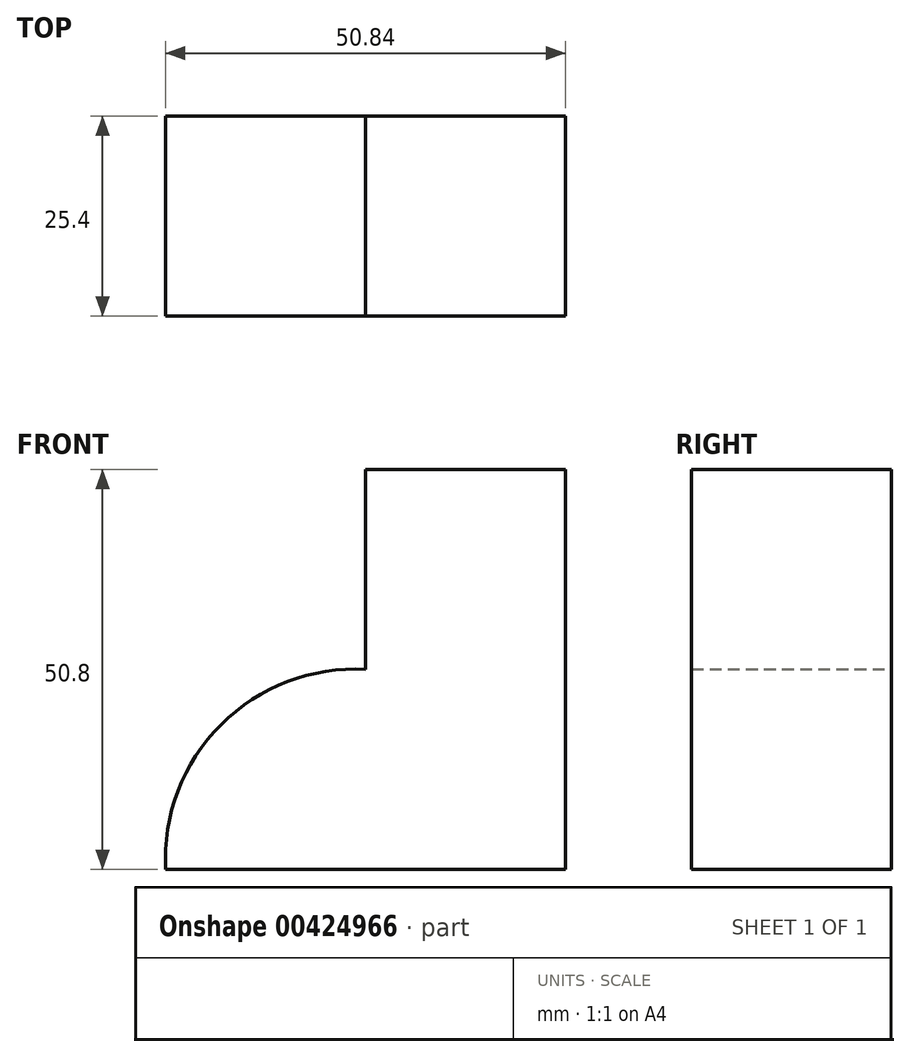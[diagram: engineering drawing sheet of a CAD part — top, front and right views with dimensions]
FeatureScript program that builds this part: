
annotation { "Feature Type Name" : "Feature", "Feature Type Description" : "" }
export const myFeature = defineFeature(function(context is Context, id is Id, definition is map)
    precondition{}
    {
        {
            var Q0;
            Q0=qCreatedBy(makeId("Front.planeOp"),FACE);
            var sketch = newSketch(context, id + "F0", { "sketchPlane" : qUnion([Q0])});
            skLineSegment(sketch, "E0", {"start": v(0, 0) * mm, "end": v(-50.8, 0) * mm});
            skLineSegment(sketch, "E1", {"start": v(0, 0) * mm, "end": v(0, 50.8) * mm});
            skLineSegment(sketch, "E2", {"start": v(0, 50.8) * mm, "end": v(-25.4, 50.8) * mm});
            skLineSegment(sketch, "E3", {"start": v(-25.4, 50.8) * mm, "end": v(-25.4, 25.4) * mm});
            skArc(sketch, "E4", {"start": v(-25.4, 25.4) * mm, "mid": v(-43.79, 18.39) * mm, "end": v(-50.8, 0) * mm});
            skSolve(sketch);
        }
        {
            var Q0;
            Q0 = qSketchRegion(id + "F0", true);
            extrude(context, id + "F1", {"entities" : qUnion([Q0]), "depth" : 25.4 * mm});
        }
    });
